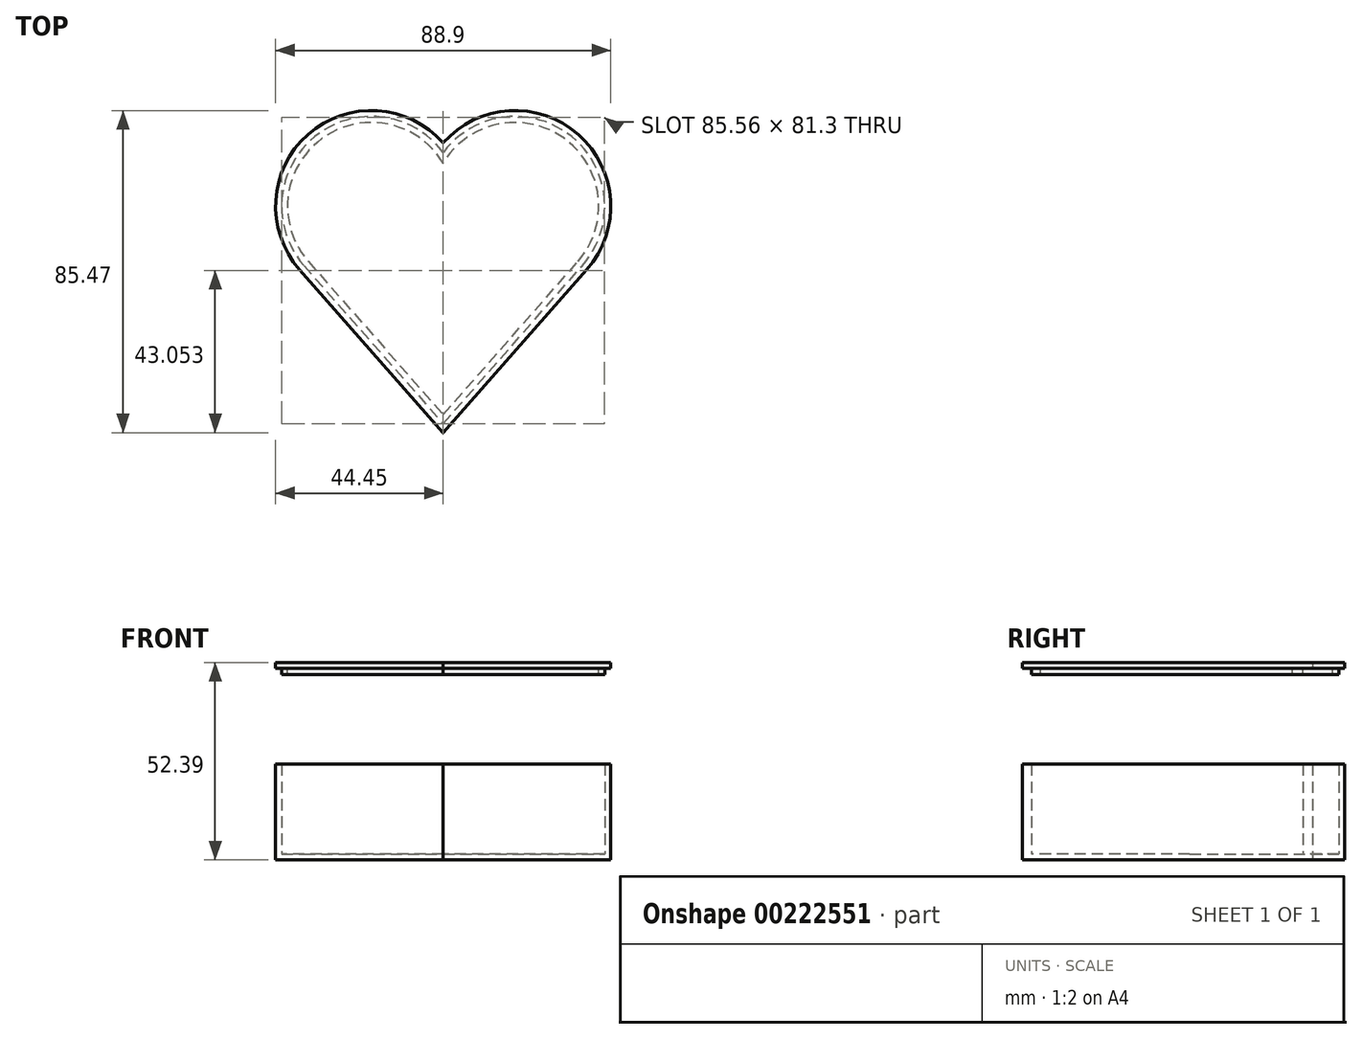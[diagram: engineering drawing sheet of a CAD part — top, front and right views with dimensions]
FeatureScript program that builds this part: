
annotation { "Feature Type Name" : "Feature", "Feature Type Description" : "" }
export const myFeature = defineFeature(function(context is Context, id is Id, definition is map)
    precondition{}
    {
        {
            var Q0;
            Q0=qCreatedBy(makeId("Top.planeOp"),FACE);
            var sketch = newSketch(context, id + "F0", { "sketchPlane" : qUnion([Q0])});
            skArc(sketch, "E0", {"start": v(0, 16.8) * mm, "mid": v(-35.84, 19.06) * mm, "end": v(-38.11, -16.79) * mm});
            skArc(sketch, "E1", {"start": v(38.11, -16.79) * mm, "mid": v(35.84, 19.06) * mm, "end": v(0, 16.8) * mm});
            skLineSegment(sketch, "E2", {"start": v(-38.11, -16.79) * mm, "end": v(0, -60.07) * mm});
            skLineSegment(sketch, "E3", {"start": v(0, -60.07) * mm, "end": v(38.11, -16.79) * mm});
            skSolve(sketch);
        }
        {
            var Q0;
            Q0 = qSketchRegion(id + "F0", true);
            extrude(context, id + "F1", {"entities" : qUnion([Q0]), "depth" : 25.4 * mm});
        }
        {
            var Q0;
            Q0=makeQuery(id+"F1.opExtrude","CAP_FACE",FACE,{"disambiguationData":[OSD([sQuery(id+"F0.wireOp",EDGE,"E0"),sQuery(id+"F0.wireOp",EDGE,"E1"),sQuery(id+"F0.wireOp",EDGE,"E2"),sQuery(id+"F0.wireOp",EDGE,"E3")])],"isStart":false});
            shell(context, id + "F2", {"entities" : qUnion([Q0]), "thickness" : 1.59 * mm});
        }
        {
            var Q0;
            Q0=makeQuery(id+"F1.opExtrude","SWEPT_BODY",BODY,{"disambiguationData":[OSD([sQuery(id+"F0.wireOp",EDGE,"E0"),sQuery(id+"F0.wireOp",EDGE,"E1"),sQuery(id+"F0.wireOp",EDGE,"E2"),sQuery(id+"F0.wireOp",EDGE,"E3")])]});
            transform(context, id + "F3", {"entities" : qUnion([Q0]), "transformType" : TransformType.TRANSLATION_3D, "dx" : 0 * mm, "dy" : 0 * mm, "dz" : 0 * mm, "makeCopy" : true});
        }
        {
            var Q0;
            Q0=makeQuery(id+"F1.opExtrude","CAP_FACE",FACE,{"disambiguationData":[OSD([sQuery(id+"F0.wireOp",EDGE,"E0"),sQuery(id+"F0.wireOp",EDGE,"E1"),sQuery(id+"F0.wireOp",EDGE,"E2"),sQuery(id+"F0.wireOp",EDGE,"E3")])],"isStart":false});
            cPlane(context, id + "F4", {"entities" : qUnion([Q0]), "cplaneType" : CPlaneType.OFFSET, "offset" : 25.4 * mm, "width" : 152.4 * mm, "height" : 152.4 * mm});
        }
        {
            var Q0;
            Q0=qCreatedBy(id+"F4.planeOp",FACE);
            var sketch = newSketch(context, id + "F5", { "sketchPlane" : qUnion([Q0])});
            skArc(sketch, "E4.0", {"start": v(0, 16.8) * mm, "mid": v(-35.84, 19.06) * mm, "end": v(-38.11, -16.79) * mm});
            skArc(sketch, "E4.1", {"start": v(38.11, -16.79) * mm, "mid": v(35.84, 19.06) * mm, "end": v(0, 16.8) * mm});
            skLineSegment(sketch, "E4.2", {"start": v(0, -60.07) * mm, "end": v(38.11, -16.79) * mm});
            skLineSegment(sketch, "E4.3", {"start": v(-38.11, -16.79) * mm, "end": v(0, -60.07) * mm});
            skSolve(sketch);
        }
        {
            var Q0;
            Q0 = qSketchRegion(id + "F5", true);
            extrude(context, id + "F6", {"entities" : qUnion([Q0]), "depth" : 1.59 * mm});
        }
        {
            var Q0;
            Q0=makeQuery(id+"F6.opExtrude","CAP_FACE",FACE,{"disambiguationData":[OSD([sQuery(id+"F5.wireOp",EDGE,"E4.0"),sQuery(id+"F5.wireOp",EDGE,"E4.1"),sQuery(id+"F5.wireOp",EDGE,"E4.2"),sQuery(id+"F5.wireOp",EDGE,"E4.3")])],"isStart":true});
            var sketch = newSketch(context, id + "F7", { "sketchPlane" : qUnion([Q0])});
            skArc(sketch, "E5.0", {"start": v(36.92, 15.74) * mm, "mid": v(34.07, -18.48) * mm, "end": v(0, -14.29) * mm});
            skArc(sketch, "E5.1", {"start": v(0, -14.29) * mm, "mid": v(-34.07, -18.48) * mm, "end": v(-36.92, 15.74) * mm});
            skLineSegment(sketch, "E5.2", {"start": v(0, 57.67) * mm, "end": v(36.92, 15.74) * mm});
            skLineSegment(sketch, "E5.3", {"start": v(-36.92, 15.74) * mm, "end": v(0, 57.67) * mm});
            skArc(sketch, "E6.0", {"start": v(0, -11.45) * mm, "mid": v(-32.17, -17.94) * mm, "end": v(-35.73, 14.69) * mm});
            skArc(sketch, "E6.1", {"start": v(35.73, 14.69) * mm, "mid": v(32.17, -17.94) * mm, "end": v(0, -11.45) * mm});
            skLineSegment(sketch, "E6.2", {"start": v(0, 55.27) * mm, "end": v(35.73, 14.69) * mm});
            skLineSegment(sketch, "E6.3", {"start": v(-35.73, 14.69) * mm, "end": v(0, 55.27) * mm});
            skSolve(sketch);
        }
        {
            var Q0;
            Q0 = qSketchRegion(id + "F7", true);
            extrude(context, id + "F8", {"entities" : qUnion([Q0]), "operationType" : NewBodyOperationType.ADD, "depth" : 1.59 * mm});
        }
    });
